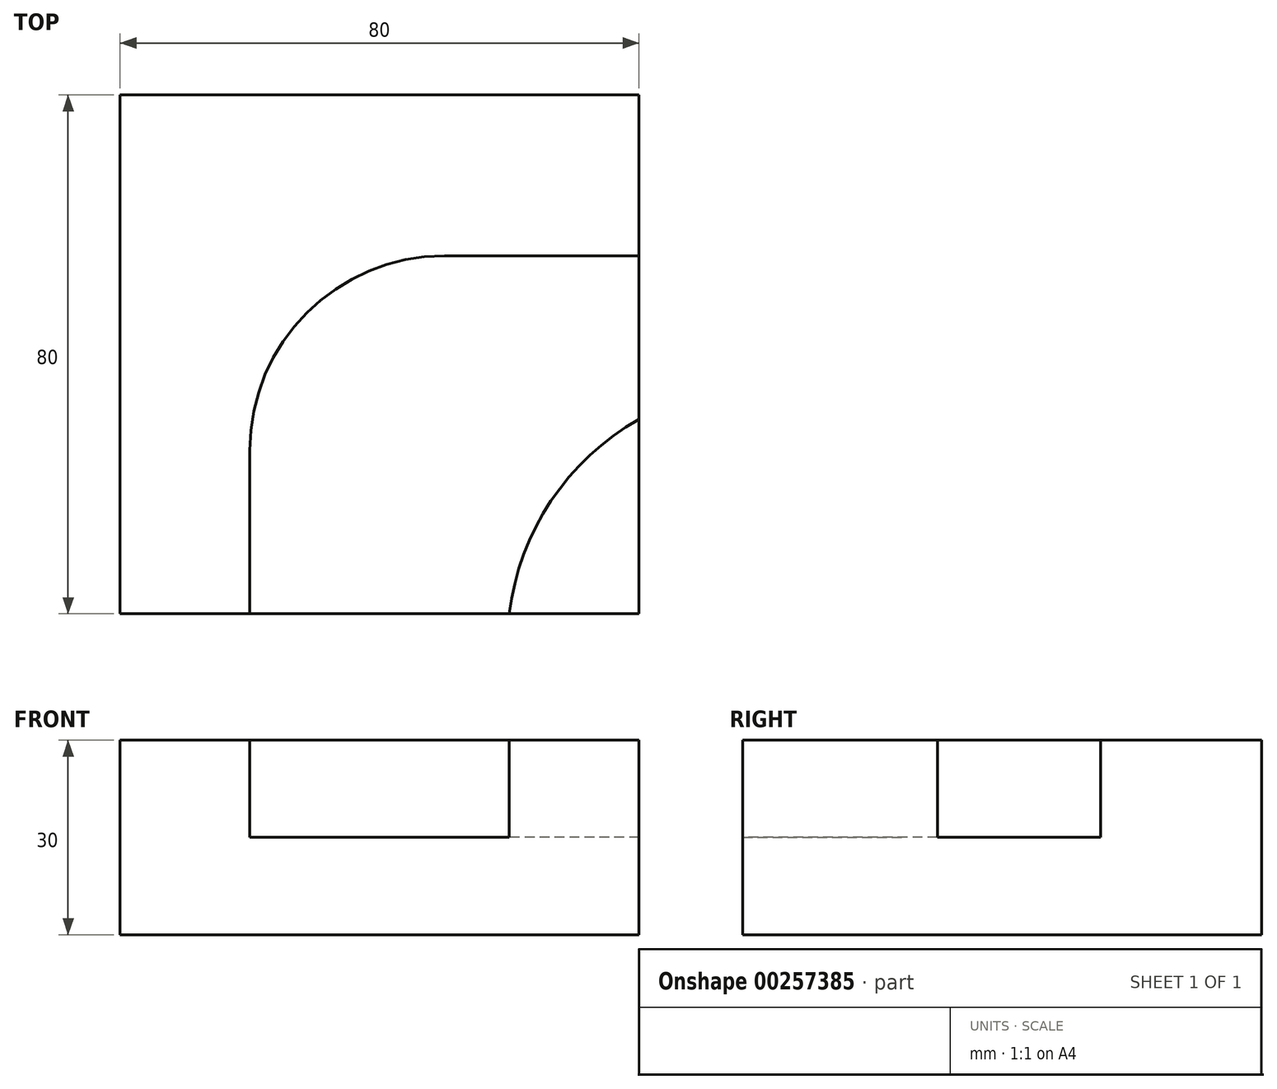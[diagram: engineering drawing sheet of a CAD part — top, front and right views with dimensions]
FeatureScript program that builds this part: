
annotation { "Feature Type Name" : "Feature", "Feature Type Description" : "" }
export const myFeature = defineFeature(function(context is Context, id is Id, definition is map)
    precondition{}
    {
        {
            var Q0;
            Q0=qCreatedBy(makeId("Top.planeOp"),FACE);
            var sketch = newSketch(context, id + "F0", { "sketchPlane" : qUnion([Q0])});
            skLineSegment(sketch, "E0.bottom", {"start": v(0, 0) * mm, "end": v(80, 0) * mm});
            skLineSegment(sketch, "E0.top", {"start": v(0, -80) * mm, "end": v(80, -80) * mm});
            skLineSegment(sketch, "E0.left", {"start": v(0, 0) * mm, "end": v(0, -80) * mm});
            skLineSegment(sketch, "E0.right", {"start": v(80, 0) * mm, "end": v(80, -80) * mm});
            skPoint(sketch, "E1", {"position": v(80, -50) * mm});
            skPoint(sketch, "E2", {"position": v(60, -80) * mm});
            skArc(sketch, "E3", {"start": v(80, -50) * mm, "mid": v(66.43, -62.62) * mm, "end": v(60, -80) * mm});
            skLineSegment(sketch, "E4", {"start": v(20, -80) * mm, "end": v(20, -54.8) * mm});
            skLineSegment(sketch, "E5", {"start": v(80, -24.8) * mm, "end": v(50, -24.8) * mm});
            skArc(sketch, "E6", {"start": v(50, -24.8) * mm, "mid": v(28.79, -33.6) * mm, "end": v(20, -54.8) * mm});
            skSolve(sketch);
        }
        {
            var Q0;
            Q0 = qSketchRegion(id + "F0", true);
            extrude(context, id + "F1", {"entities" : qUnion([Q0]), "oppositeDirection" : true, "depth" : 30 * mm});
        }
        {
            var Q0;
            {var subQ1=sQuery(id+"F0.wireOp",EDGE,"E3");Q0=makeQuery(id+"F0.imprint","IMPRINT",FACE,{"disambiguationData":[TD([[makeQuery(id+"F0.imprint","IMPRINT",EDGE,{"derivedFrom":subQ1}),-1.0]])]});}
            extrude(context, id + "F2", {"entities" : qUnion([Q0]), "operationType" : NewBodyOperationType.REMOVE, "oppositeDirection" : true, "depth" : 15 * mm});
        }
    });
